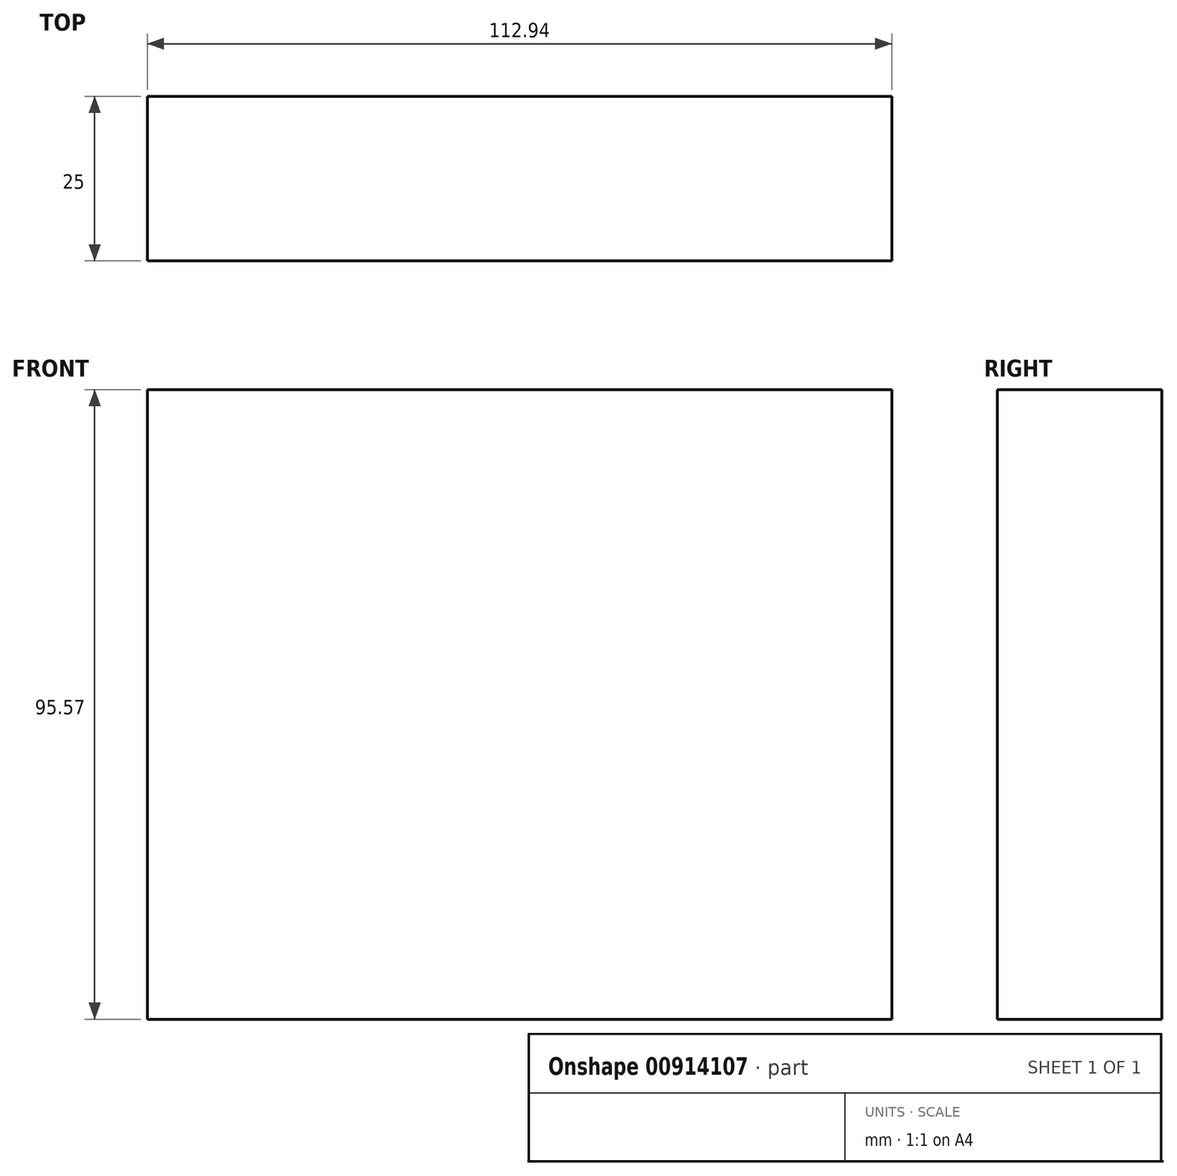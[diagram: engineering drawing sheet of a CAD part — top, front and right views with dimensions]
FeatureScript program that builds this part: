
annotation { "Feature Type Name" : "Feature", "Feature Type Description" : "" }
export const myFeature = defineFeature(function(context is Context, id is Id, definition is map)
    precondition{}
    {
        {
            var Q0;
            Q0=qCreatedBy(makeId("Front.planeOp"),FACE);
            var sketch = newSketch(context, id + "F0", { "sketchPlane" : qUnion([Q0])});
            skLineSegment(sketch, "E0.bottom", {"start": v(-213.72, -24.2) * mm, "end": v(-100.78, -24.2) * mm});
            skLineSegment(sketch, "E0.top", {"start": v(-213.72, 71.36) * mm, "end": v(-100.78, 71.36) * mm});
            skLineSegment(sketch, "E0.left", {"start": v(-213.72, -24.2) * mm, "end": v(-213.72, 71.36) * mm});
            skLineSegment(sketch, "E0.right", {"start": v(-100.78, -24.2) * mm, "end": v(-100.78, 71.36) * mm});
            skPoint(sketch, "E0.middle", {"position": v(-157.25, 23.57) * mm});
            skSolve(sketch);
        }
        {
            var Q0;
            Q0=makeQuery(id+"F0.imprint","IMPRINT",FACE,{"disambiguationData":[TD([[makeQuery(id+"F0.imprint","IMPRINT",EDGE,{"derivedFrom":sQuery(id+"F0.wireOp",EDGE,"E0.bottom")}),1.0]])]});
            extrude(context, id + "F1", {"entities" : qUnion([Q0]), "depth" : 25 * mm, "offsetDistance" : 25 * mm});
        }
    });
